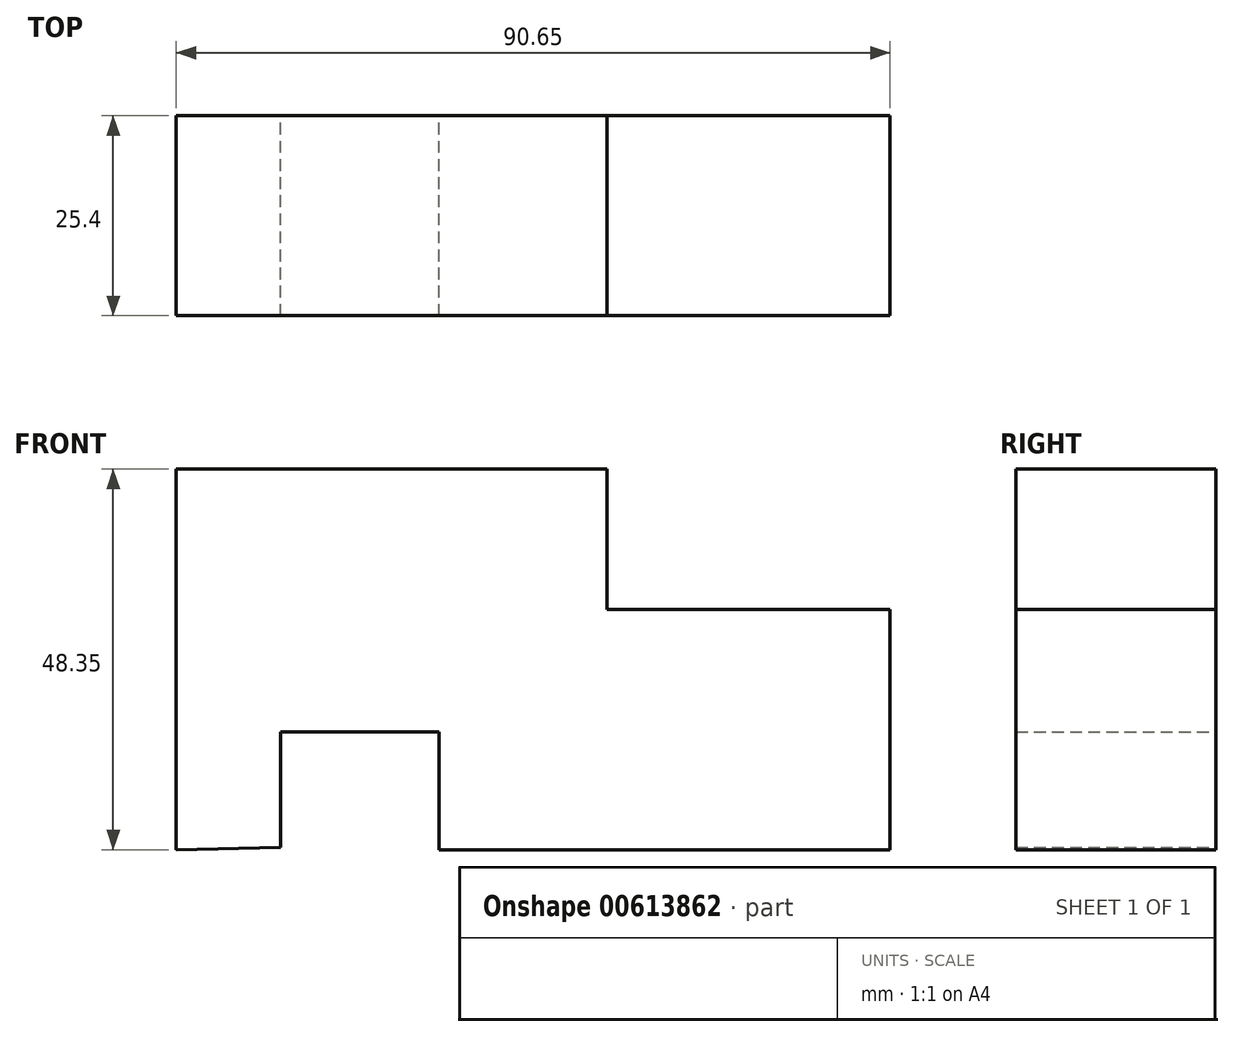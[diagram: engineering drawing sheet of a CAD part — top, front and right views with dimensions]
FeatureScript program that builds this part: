
annotation { "Feature Type Name" : "Feature", "Feature Type Description" : "" }
export const myFeature = defineFeature(function(context is Context, id is Id, definition is map)
    precondition{}
    {
        {
            var Q0;
            Q0=qCreatedBy(makeId("Front.planeOp"),FACE);
            var sketch = newSketch(context, id + "F0", { "sketchPlane" : qUnion([Q0])});
            skLineSegment(sketch, "E0", {"start": v(-59.14, 7.63) * mm, "end": v(-59.14, 55.98) * mm});
            skLineSegment(sketch, "E1", {"start": v(-59.14, 55.98) * mm, "end": v(-4.46, 55.98) * mm});
            skLineSegment(sketch, "E2", {"start": v(-4.46, 55.98) * mm, "end": v(-4.46, 38.13) * mm});
            skLineSegment(sketch, "E3", {"start": v(-4.46, 38.13) * mm, "end": v(31.51, 38.13) * mm});
            skLineSegment(sketch, "E4", {"start": v(31.51, 38.13) * mm, "end": v(31.51, 7.63) * mm});
            skLineSegment(sketch, "E5", {"start": v(31.51, 7.63) * mm, "end": v(-25.76, 7.63) * mm});
            skLineSegment(sketch, "E6", {"start": v(-25.76, 7.63) * mm, "end": v(-25.76, 22.6) * mm});
            skLineSegment(sketch, "E7", {"start": v(-25.76, 22.6) * mm, "end": v(-45.9, 22.6) * mm});
            skLineSegment(sketch, "E8", {"start": v(-45.9, 22.6) * mm, "end": v(-45.9, 7.91) * mm});
            skLineSegment(sketch, "E9", {"start": v(-45.9, 7.91) * mm, "end": v(-59.14, 7.63) * mm});
            skSolve(sketch);
        }
        {
            var Q0;
            Q0 = qSketchRegion(id + "F0", true);
            extrude(context, id + "F1", {"entities" : qUnion([Q0]), "depth" : 25.4 * mm, "offsetDistance" : 25.4 * mm});
        }
    });
